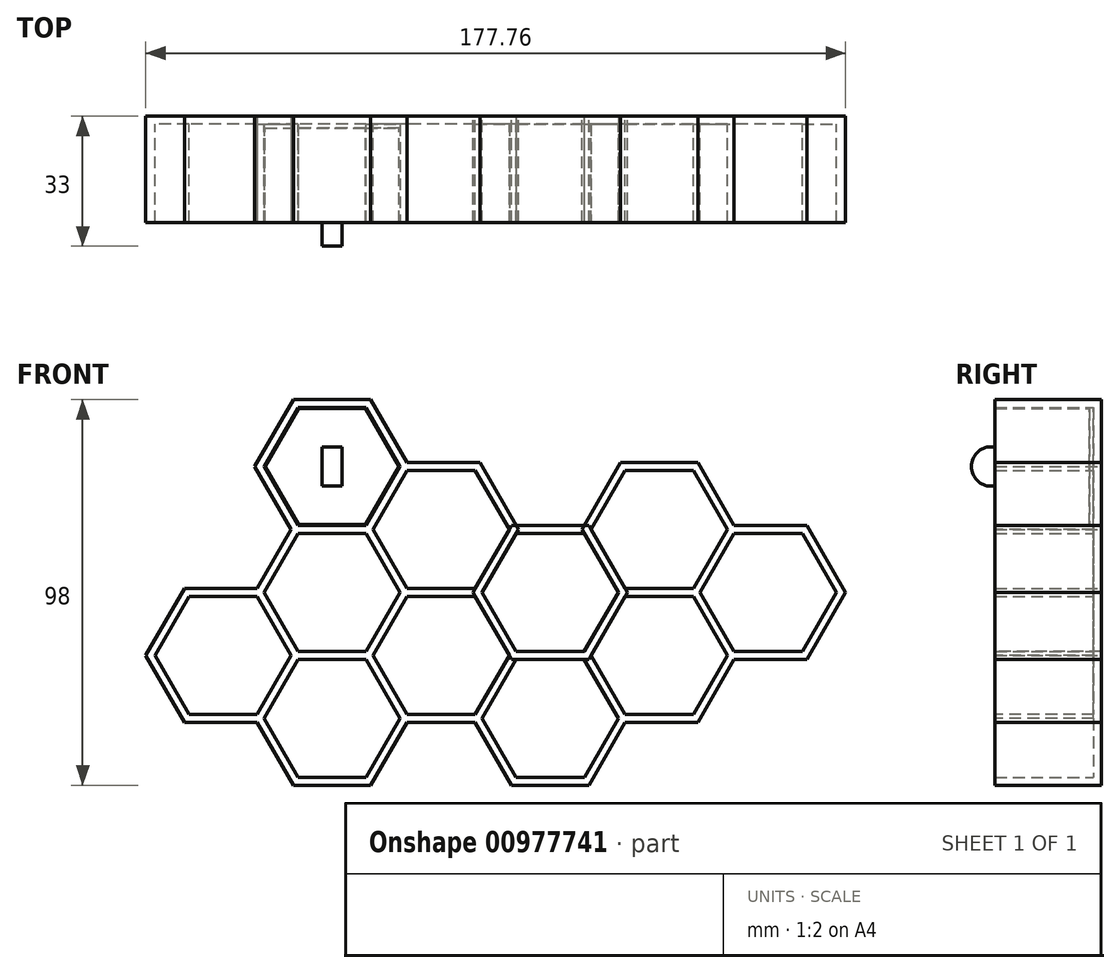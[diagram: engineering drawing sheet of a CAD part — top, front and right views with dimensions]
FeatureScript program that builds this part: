
annotation { "Feature Type Name" : "Feature", "Feature Type Description" : "" }
export const myFeature = defineFeature(function(context is Context, id is Id, definition is map)
    precondition{}
    {
        {
            var Q0;
            Q0=qCreatedBy(makeId("Front.planeOp"),FACE);
            var sketch = newSketch(context, id + "F0", { "sketchPlane" : qUnion([Q0])});
            skCircle(sketch, "E0.cCircle", {"center": v(0, 0) * mm, "radius": 15 * mm, "construction": true});
            skLineSegment(sketch, "E0.0", {"start": v(17.32, 0) * mm, "end": v(8.66, -15) * mm});
            skLineSegment(sketch, "E0.1", {"start": v(8.66, -15) * mm, "end": v(-8.66, -15) * mm});
            skLineSegment(sketch, "E0.2", {"start": v(-8.66, -15) * mm, "end": v(-17.32, 0) * mm});
            skLineSegment(sketch, "E0.3", {"start": v(-17.32, 0) * mm, "end": v(-8.66, 15) * mm});
            skLineSegment(sketch, "E0.4", {"start": v(-8.66, 15) * mm, "end": v(8.66, 15) * mm});
            skLineSegment(sketch, "E0.5", {"start": v(8.66, 15) * mm, "end": v(17.32, 0) * mm});
            skPoint(sketch, "E0.0.midPoint", {"position": v(13, -7.5) * mm});
            skLineSegment(sketch, "E1.0", {"start": v(-9.81, 17) * mm, "end": v(9.81, 17) * mm});
            skLineSegment(sketch, "E1.1", {"start": v(19.63, 0) * mm, "end": v(9.81, -17) * mm});
            skLineSegment(sketch, "E1.2", {"start": v(9.81, -17) * mm, "end": v(-9.81, -17) * mm});
            skLineSegment(sketch, "E1.3", {"start": v(9.81, 17) * mm, "end": v(19.63, 0) * mm});
            skLineSegment(sketch, "E1.4", {"start": v(-9.81, -17) * mm, "end": v(-19.63, 0) * mm});
            skLineSegment(sketch, "E1.5", {"start": v(-19.63, 0) * mm, "end": v(-9.81, 17) * mm});
            skSolve(sketch);
        }
        {
            var Q0;
            Q0 = qSketchRegion(id + "F0", true);
            extrude(context, id + "F1", {"entities" : qUnion([Q0]), "depth" : 25 * mm, "offsetDistance" : 25 * mm});
        }
        {
            var Q0;
            Q0=makeQuery(id+"F1.opExtrude","CAP_FACE",FACE,{"disambiguationData":[OSD([sQuery(id+"F0.wireOp",EDGE,"E0.0"),sQuery(id+"F0.wireOp",EDGE,"E0.1"),sQuery(id+"F0.wireOp",EDGE,"E0.2"),sQuery(id+"F0.wireOp",EDGE,"E0.3"),sQuery(id+"F0.wireOp",EDGE,"E0.4"),sQuery(id+"F0.wireOp",EDGE,"E0.5"),sQuery(id+"F0.wireOp",EDGE,"E1.0"),sQuery(id+"F0.wireOp",EDGE,"E1.1"),sQuery(id+"F0.wireOp",EDGE,"E1.2"),sQuery(id+"F0.wireOp",EDGE,"E1.3"),sQuery(id+"F0.wireOp",EDGE,"E1.4"),sQuery(id+"F0.wireOp",EDGE,"E1.5")])],"isStart":true});
            var Q1;
            Q1=makeQuery(id+"F0.imprint","IMPRINT",FACE,{"disambiguationData":[TD([[makeQuery(id+"F0.imprint","IMPRINT",EDGE,{"derivedFrom":sQuery(id+"F0.wireOp",EDGE,"E0.0")}),-1.0]])]});
            extrude(context, id + "F2", {"entities" : qUnion([Q0, Q1]), "operationType" : NewBodyOperationType.ADD, "depth" : 2 * mm, "offsetDistance" : 25 * mm});
        }
        {
            var Q0;
            Q0=makeQuery(id+"F1.opExtrude","SWEPT_BODY",BODY,{"disambiguationData":[OSD([sQuery(id+"F0.wireOp",EDGE,"E0.0"),sQuery(id+"F0.wireOp",EDGE,"E0.1"),sQuery(id+"F0.wireOp",EDGE,"E0.2"),sQuery(id+"F0.wireOp",EDGE,"E0.3"),sQuery(id+"F0.wireOp",EDGE,"E0.4"),sQuery(id+"F0.wireOp",EDGE,"E0.5"),sQuery(id+"F0.wireOp",EDGE,"E1.0"),sQuery(id+"F0.wireOp",EDGE,"E1.1"),sQuery(id+"F0.wireOp",EDGE,"E1.2"),sQuery(id+"F0.wireOp",EDGE,"E1.3"),sQuery(id+"F0.wireOp",EDGE,"E1.4"),sQuery(id+"F0.wireOp",EDGE,"E1.5")])]});
            transform(context, id + "F3", {"entities" : qUnion([Q0]), "transformType" : TransformType.TRANSLATION_3D, "dx" : 27.7 * mm, "dy" : 0 * mm, "dz" : 16 * mm, "makeCopy" : true});
        }
        {
            var Q0;
            Q0=makeQuery(id+"F1.opExtrude","SWEPT_BODY",BODY,{"disambiguationData":[OSD([sQuery(id+"F0.wireOp",EDGE,"E0.0"),sQuery(id+"F0.wireOp",EDGE,"E0.1"),sQuery(id+"F0.wireOp",EDGE,"E0.2"),sQuery(id+"F0.wireOp",EDGE,"E0.3"),sQuery(id+"F0.wireOp",EDGE,"E0.4"),sQuery(id+"F0.wireOp",EDGE,"E0.5"),sQuery(id+"F0.wireOp",EDGE,"E1.0"),sQuery(id+"F0.wireOp",EDGE,"E1.1"),sQuery(id+"F0.wireOp",EDGE,"E1.2"),sQuery(id+"F0.wireOp",EDGE,"E1.3"),sQuery(id+"F0.wireOp",EDGE,"E1.4"),sQuery(id+"F0.wireOp",EDGE,"E1.5")])]});
            transform(context, id + "F4", {"entities" : qUnion([Q0]), "transformType" : TransformType.TRANSLATION_3D, "dx" : 27.7 * mm, "dy" : 0 * mm, "dz" : -16 * mm, "makeCopy" : true});
        }
        {
            var Q0;
            Q0=makeQuery(id+"F1.opExtrude","SWEPT_BODY",BODY,{"disambiguationData":[OSD([sQuery(id+"F0.wireOp",EDGE,"E0.0"),sQuery(id+"F0.wireOp",EDGE,"E0.1"),sQuery(id+"F0.wireOp",EDGE,"E0.2"),sQuery(id+"F0.wireOp",EDGE,"E0.3"),sQuery(id+"F0.wireOp",EDGE,"E0.4"),sQuery(id+"F0.wireOp",EDGE,"E0.5"),sQuery(id+"F0.wireOp",EDGE,"E1.0"),sQuery(id+"F0.wireOp",EDGE,"E1.1"),sQuery(id+"F0.wireOp",EDGE,"E1.2"),sQuery(id+"F0.wireOp",EDGE,"E1.3"),sQuery(id+"F0.wireOp",EDGE,"E1.4"),sQuery(id+"F0.wireOp",EDGE,"E1.5")])]});
            transform(context, id + "F5", {"entities" : qUnion([Q0]), "transformType" : TransformType.TRANSLATION_3D, "dx" : -27.7 * mm, "dy" : 0 * mm, "dz" : -16 * mm, "makeCopy" : true});
        }
        {
            var Q0;
            Q0=makeQuery(id+"F1.opExtrude","SWEPT_BODY",BODY,{"disambiguationData":[OSD([sQuery(id+"F0.wireOp",EDGE,"E0.0"),sQuery(id+"F0.wireOp",EDGE,"E0.1"),sQuery(id+"F0.wireOp",EDGE,"E0.2"),sQuery(id+"F0.wireOp",EDGE,"E0.3"),sQuery(id+"F0.wireOp",EDGE,"E0.4"),sQuery(id+"F0.wireOp",EDGE,"E0.5"),sQuery(id+"F0.wireOp",EDGE,"E1.0"),sQuery(id+"F0.wireOp",EDGE,"E1.1"),sQuery(id+"F0.wireOp",EDGE,"E1.2"),sQuery(id+"F0.wireOp",EDGE,"E1.3"),sQuery(id+"F0.wireOp",EDGE,"E1.4"),sQuery(id+"F0.wireOp",EDGE,"E1.5")])]});
            transform(context, id + "F6", {"entities" : qUnion([Q0]), "transformType" : TransformType.TRANSLATION_3D, "dx" : -27.7 * mm, "dy" : 0 * mm, "dz" : 16 * mm, "makeCopy" : true});
        }
        {
            var Q0;
            Q0=makeQuery(id+"F1.opExtrude","SWEPT_BODY",BODY,{"disambiguationData":[OSD([sQuery(id+"F0.wireOp",EDGE,"E0.0"),sQuery(id+"F0.wireOp",EDGE,"E0.1"),sQuery(id+"F0.wireOp",EDGE,"E0.2"),sQuery(id+"F0.wireOp",EDGE,"E0.3"),sQuery(id+"F0.wireOp",EDGE,"E0.4"),sQuery(id+"F0.wireOp",EDGE,"E0.5"),sQuery(id+"F0.wireOp",EDGE,"E1.0"),sQuery(id+"F0.wireOp",EDGE,"E1.1"),sQuery(id+"F0.wireOp",EDGE,"E1.2"),sQuery(id+"F0.wireOp",EDGE,"E1.3"),sQuery(id+"F0.wireOp",EDGE,"E1.4"),sQuery(id+"F0.wireOp",EDGE,"E1.5")])]});
            transform(context, id + "F7", {"entities" : qUnion([Q0]), "transformType" : TransformType.TRANSLATION_3D, "dx" : 0 * mm, "dy" : 0 * mm, "dz" : 32 * mm, "makeCopy" : true});
        }
        {
            var Q0;
            Q0=makeQuery(id+"F3.opPattern","COPY",BODY,{"derivedFrom":makeQuery(id+"F1.opExtrude","SWEPT_BODY",BODY,{"disambiguationData":[OSD([sQuery(id+"F0.wireOp",EDGE,"E0.0"),sQuery(id+"F0.wireOp",EDGE,"E0.1"),sQuery(id+"F0.wireOp",EDGE,"E0.2"),sQuery(id+"F0.wireOp",EDGE,"E0.3"),sQuery(id+"F0.wireOp",EDGE,"E0.4"),sQuery(id+"F0.wireOp",EDGE,"E0.5"),sQuery(id+"F0.wireOp",EDGE,"E1.0"),sQuery(id+"F0.wireOp",EDGE,"E1.1"),sQuery(id+"F0.wireOp",EDGE,"E1.2"),sQuery(id+"F0.wireOp",EDGE,"E1.3"),sQuery(id+"F0.wireOp",EDGE,"E1.4"),sQuery(id+"F0.wireOp",EDGE,"E1.5")])]}),"instanceName":"1"});
            transform(context, id + "F8", {"entities" : qUnion([Q0]), "transformType" : TransformType.TRANSLATION_3D, "dx" : 27.7 * mm, "dy" : 0 * mm, "dz" : -16 * mm, "makeCopy" : true});
        }
        {
            var Q0;
            Q0=makeQuery(id+"F7.opPattern","COPY",BODY,{"derivedFrom":makeQuery(id+"F1.opExtrude","SWEPT_BODY",BODY,{"disambiguationData":[OSD([sQuery(id+"F0.wireOp",EDGE,"E0.0"),sQuery(id+"F0.wireOp",EDGE,"E0.1"),sQuery(id+"F0.wireOp",EDGE,"E0.2"),sQuery(id+"F0.wireOp",EDGE,"E0.3"),sQuery(id+"F0.wireOp",EDGE,"E0.4"),sQuery(id+"F0.wireOp",EDGE,"E0.5"),sQuery(id+"F0.wireOp",EDGE,"E1.0"),sQuery(id+"F0.wireOp",EDGE,"E1.1"),sQuery(id+"F0.wireOp",EDGE,"E1.2"),sQuery(id+"F0.wireOp",EDGE,"E1.3"),sQuery(id+"F0.wireOp",EDGE,"E1.4"),sQuery(id+"F0.wireOp",EDGE,"E1.5")])]}),"instanceName":"1"});
            transform(context, id + "F9", {"entities" : qUnion([Q0]), "transformType" : TransformType.TRANSLATION_3D, "dx" : -27.7 * mm, "dy" : 0 * mm, "dz" : 16 * mm, "makeCopy" : true});
        }
        {
            var Q0;
            Q0=makeQuery(id+"F3.opPattern","COPY",BODY,{"derivedFrom":makeQuery(id+"F1.opExtrude","SWEPT_BODY",BODY,{"disambiguationData":[OSD([sQuery(id+"F0.wireOp",EDGE,"E0.0"),sQuery(id+"F0.wireOp",EDGE,"E0.1"),sQuery(id+"F0.wireOp",EDGE,"E0.2"),sQuery(id+"F0.wireOp",EDGE,"E0.3"),sQuery(id+"F0.wireOp",EDGE,"E0.4"),sQuery(id+"F0.wireOp",EDGE,"E0.5"),sQuery(id+"F0.wireOp",EDGE,"E1.0"),sQuery(id+"F0.wireOp",EDGE,"E1.1"),sQuery(id+"F0.wireOp",EDGE,"E1.2"),sQuery(id+"F0.wireOp",EDGE,"E1.3"),sQuery(id+"F0.wireOp",EDGE,"E1.4"),sQuery(id+"F0.wireOp",EDGE,"E1.5")])]}),"instanceName":"1"});
            transform(context, id + "F10", {"entities" : qUnion([Q0]), "transformType" : TransformType.TRANSLATION_3D, "dx" : 27.7 * mm, "dy" : 0 * mm, "dz" : 16 * mm, "makeCopy" : true});
        }
        {
            var Q0;
            Q0=makeQuery(id+"F6.opPattern","COPY",BODY,{"derivedFrom":makeQuery(id+"F1.opExtrude","SWEPT_BODY",BODY,{"disambiguationData":[OSD([sQuery(id+"F0.wireOp",EDGE,"E0.0"),sQuery(id+"F0.wireOp",EDGE,"E0.1"),sQuery(id+"F0.wireOp",EDGE,"E0.2"),sQuery(id+"F0.wireOp",EDGE,"E0.3"),sQuery(id+"F0.wireOp",EDGE,"E0.4"),sQuery(id+"F0.wireOp",EDGE,"E0.5"),sQuery(id+"F0.wireOp",EDGE,"E1.0"),sQuery(id+"F0.wireOp",EDGE,"E1.1"),sQuery(id+"F0.wireOp",EDGE,"E1.2"),sQuery(id+"F0.wireOp",EDGE,"E1.3"),sQuery(id+"F0.wireOp",EDGE,"E1.4"),sQuery(id+"F0.wireOp",EDGE,"E1.5")])]}),"instanceName":"1"});
            transform(context, id + "F11", {"entities" : qUnion([Q0]), "transformType" : TransformType.TRANSLATION_3D, "dx" : -27.7 * mm, "dy" : 0 * mm, "dz" : -16 * mm, "makeCopy" : true});
        }
        {
            var Q0;
            Q0=makeQuery(id+"F10.opPattern","COPY",BODY,{"derivedFrom":makeQuery(id+"F3.opPattern","COPY",BODY,{"derivedFrom":makeQuery(id+"F1.opExtrude","SWEPT_BODY",BODY,{"disambiguationData":[OSD([sQuery(id+"F0.wireOp",EDGE,"E0.0"),sQuery(id+"F0.wireOp",EDGE,"E0.1"),sQuery(id+"F0.wireOp",EDGE,"E0.2"),sQuery(id+"F0.wireOp",EDGE,"E0.3"),sQuery(id+"F0.wireOp",EDGE,"E0.4"),sQuery(id+"F0.wireOp",EDGE,"E0.5"),sQuery(id+"F0.wireOp",EDGE,"E1.0"),sQuery(id+"F0.wireOp",EDGE,"E1.1"),sQuery(id+"F0.wireOp",EDGE,"E1.2"),sQuery(id+"F0.wireOp",EDGE,"E1.3"),sQuery(id+"F0.wireOp",EDGE,"E1.4"),sQuery(id+"F0.wireOp",EDGE,"E1.5")])]}),"instanceName":"1"}),"instanceName":"1"});
            transform(context, id + "F12", {"entities" : qUnion([Q0]), "transformType" : TransformType.TRANSLATION_3D, "dx" : 27.7 * mm, "dy" : 0 * mm, "dz" : -16 * mm, "makeCopy" : true});
        }
        {
            var Q0;
            Q0=makeQuery(id+"F1.opExtrude","SWEPT_BODY",BODY,{"disambiguationData":[OSD([sQuery(id+"F0.wireOp",EDGE,"E0.0"),sQuery(id+"F0.wireOp",EDGE,"E0.1"),sQuery(id+"F0.wireOp",EDGE,"E0.2"),sQuery(id+"F0.wireOp",EDGE,"E0.3"),sQuery(id+"F0.wireOp",EDGE,"E0.4"),sQuery(id+"F0.wireOp",EDGE,"E0.5"),sQuery(id+"F0.wireOp",EDGE,"E1.0"),sQuery(id+"F0.wireOp",EDGE,"E1.1"),sQuery(id+"F0.wireOp",EDGE,"E1.2"),sQuery(id+"F0.wireOp",EDGE,"E1.3"),sQuery(id+"F0.wireOp",EDGE,"E1.4"),sQuery(id+"F0.wireOp",EDGE,"E1.5")])]});
            var Q1;
            Q1=makeQuery(id+"F4.opPattern","COPY",BODY,{"derivedFrom":makeQuery(id+"F1.opExtrude","SWEPT_BODY",BODY,{"disambiguationData":[OSD([sQuery(id+"F0.wireOp",EDGE,"E0.0"),sQuery(id+"F0.wireOp",EDGE,"E0.1"),sQuery(id+"F0.wireOp",EDGE,"E0.2"),sQuery(id+"F0.wireOp",EDGE,"E0.3"),sQuery(id+"F0.wireOp",EDGE,"E0.4"),sQuery(id+"F0.wireOp",EDGE,"E0.5"),sQuery(id+"F0.wireOp",EDGE,"E1.0"),sQuery(id+"F0.wireOp",EDGE,"E1.1"),sQuery(id+"F0.wireOp",EDGE,"E1.2"),sQuery(id+"F0.wireOp",EDGE,"E1.3"),sQuery(id+"F0.wireOp",EDGE,"E1.4"),sQuery(id+"F0.wireOp",EDGE,"E1.5")])]}),"instanceName":"1"});
            var Q2;
            Q2=makeQuery(id+"F5.opPattern","COPY",BODY,{"derivedFrom":makeQuery(id+"F1.opExtrude","SWEPT_BODY",BODY,{"disambiguationData":[OSD([sQuery(id+"F0.wireOp",EDGE,"E0.0"),sQuery(id+"F0.wireOp",EDGE,"E0.1"),sQuery(id+"F0.wireOp",EDGE,"E0.2"),sQuery(id+"F0.wireOp",EDGE,"E0.3"),sQuery(id+"F0.wireOp",EDGE,"E0.4"),sQuery(id+"F0.wireOp",EDGE,"E0.5"),sQuery(id+"F0.wireOp",EDGE,"E1.0"),sQuery(id+"F0.wireOp",EDGE,"E1.1"),sQuery(id+"F0.wireOp",EDGE,"E1.2"),sQuery(id+"F0.wireOp",EDGE,"E1.3"),sQuery(id+"F0.wireOp",EDGE,"E1.4"),sQuery(id+"F0.wireOp",EDGE,"E1.5")])]}),"instanceName":"1"});
            var Q3;
            Q3=makeQuery(id+"F6.opPattern","COPY",BODY,{"derivedFrom":makeQuery(id+"F1.opExtrude","SWEPT_BODY",BODY,{"disambiguationData":[OSD([sQuery(id+"F0.wireOp",EDGE,"E0.0"),sQuery(id+"F0.wireOp",EDGE,"E0.1"),sQuery(id+"F0.wireOp",EDGE,"E0.2"),sQuery(id+"F0.wireOp",EDGE,"E0.3"),sQuery(id+"F0.wireOp",EDGE,"E0.4"),sQuery(id+"F0.wireOp",EDGE,"E0.5"),sQuery(id+"F0.wireOp",EDGE,"E1.0"),sQuery(id+"F0.wireOp",EDGE,"E1.1"),sQuery(id+"F0.wireOp",EDGE,"E1.2"),sQuery(id+"F0.wireOp",EDGE,"E1.3"),sQuery(id+"F0.wireOp",EDGE,"E1.4"),sQuery(id+"F0.wireOp",EDGE,"E1.5")])]}),"instanceName":"1"});
            var Q4;
            Q4=makeQuery(id+"F7.opPattern","COPY",BODY,{"derivedFrom":makeQuery(id+"F1.opExtrude","SWEPT_BODY",BODY,{"disambiguationData":[OSD([sQuery(id+"F0.wireOp",EDGE,"E0.0"),sQuery(id+"F0.wireOp",EDGE,"E0.1"),sQuery(id+"F0.wireOp",EDGE,"E0.2"),sQuery(id+"F0.wireOp",EDGE,"E0.3"),sQuery(id+"F0.wireOp",EDGE,"E0.4"),sQuery(id+"F0.wireOp",EDGE,"E0.5"),sQuery(id+"F0.wireOp",EDGE,"E1.0"),sQuery(id+"F0.wireOp",EDGE,"E1.1"),sQuery(id+"F0.wireOp",EDGE,"E1.2"),sQuery(id+"F0.wireOp",EDGE,"E1.3"),sQuery(id+"F0.wireOp",EDGE,"E1.4"),sQuery(id+"F0.wireOp",EDGE,"E1.5")])]}),"instanceName":"1"});
            var Q5;
            Q5=makeQuery(id+"F9.opPattern","COPY",BODY,{"derivedFrom":makeQuery(id+"F7.opPattern","COPY",BODY,{"derivedFrom":makeQuery(id+"F1.opExtrude","SWEPT_BODY",BODY,{"disambiguationData":[OSD([sQuery(id+"F0.wireOp",EDGE,"E0.0"),sQuery(id+"F0.wireOp",EDGE,"E0.1"),sQuery(id+"F0.wireOp",EDGE,"E0.2"),sQuery(id+"F0.wireOp",EDGE,"E0.3"),sQuery(id+"F0.wireOp",EDGE,"E0.4"),sQuery(id+"F0.wireOp",EDGE,"E0.5"),sQuery(id+"F0.wireOp",EDGE,"E1.0"),sQuery(id+"F0.wireOp",EDGE,"E1.1"),sQuery(id+"F0.wireOp",EDGE,"E1.2"),sQuery(id+"F0.wireOp",EDGE,"E1.3"),sQuery(id+"F0.wireOp",EDGE,"E1.4"),sQuery(id+"F0.wireOp",EDGE,"E1.5")])]}),"instanceName":"1"}),"instanceName":"1"});
            var Q6;
            Q6=makeQuery(id+"F8.opPattern","COPY",BODY,{"derivedFrom":makeQuery(id+"F3.opPattern","COPY",BODY,{"derivedFrom":makeQuery(id+"F1.opExtrude","SWEPT_BODY",BODY,{"disambiguationData":[OSD([sQuery(id+"F0.wireOp",EDGE,"E0.0"),sQuery(id+"F0.wireOp",EDGE,"E0.1"),sQuery(id+"F0.wireOp",EDGE,"E0.2"),sQuery(id+"F0.wireOp",EDGE,"E0.3"),sQuery(id+"F0.wireOp",EDGE,"E0.4"),sQuery(id+"F0.wireOp",EDGE,"E0.5"),sQuery(id+"F0.wireOp",EDGE,"E1.0"),sQuery(id+"F0.wireOp",EDGE,"E1.1"),sQuery(id+"F0.wireOp",EDGE,"E1.2"),sQuery(id+"F0.wireOp",EDGE,"E1.3"),sQuery(id+"F0.wireOp",EDGE,"E1.4"),sQuery(id+"F0.wireOp",EDGE,"E1.5")])]}),"instanceName":"1"}),"instanceName":"1"});
            var Q7;
            Q7=makeQuery(id+"F10.opPattern","COPY",BODY,{"derivedFrom":makeQuery(id+"F3.opPattern","COPY",BODY,{"derivedFrom":makeQuery(id+"F1.opExtrude","SWEPT_BODY",BODY,{"disambiguationData":[OSD([sQuery(id+"F0.wireOp",EDGE,"E0.0"),sQuery(id+"F0.wireOp",EDGE,"E0.1"),sQuery(id+"F0.wireOp",EDGE,"E0.2"),sQuery(id+"F0.wireOp",EDGE,"E0.3"),sQuery(id+"F0.wireOp",EDGE,"E0.4"),sQuery(id+"F0.wireOp",EDGE,"E0.5"),sQuery(id+"F0.wireOp",EDGE,"E1.0"),sQuery(id+"F0.wireOp",EDGE,"E1.1"),sQuery(id+"F0.wireOp",EDGE,"E1.2"),sQuery(id+"F0.wireOp",EDGE,"E1.3"),sQuery(id+"F0.wireOp",EDGE,"E1.4"),sQuery(id+"F0.wireOp",EDGE,"E1.5")])]}),"instanceName":"1"}),"instanceName":"1"});
            var Q8;
            Q8=makeQuery(id+"F11.opPattern","COPY",BODY,{"derivedFrom":makeQuery(id+"F6.opPattern","COPY",BODY,{"derivedFrom":makeQuery(id+"F1.opExtrude","SWEPT_BODY",BODY,{"disambiguationData":[OSD([sQuery(id+"F0.wireOp",EDGE,"E0.0"),sQuery(id+"F0.wireOp",EDGE,"E0.1"),sQuery(id+"F0.wireOp",EDGE,"E0.2"),sQuery(id+"F0.wireOp",EDGE,"E0.3"),sQuery(id+"F0.wireOp",EDGE,"E0.4"),sQuery(id+"F0.wireOp",EDGE,"E0.5"),sQuery(id+"F0.wireOp",EDGE,"E1.0"),sQuery(id+"F0.wireOp",EDGE,"E1.1"),sQuery(id+"F0.wireOp",EDGE,"E1.2"),sQuery(id+"F0.wireOp",EDGE,"E1.3"),sQuery(id+"F0.wireOp",EDGE,"E1.4"),sQuery(id+"F0.wireOp",EDGE,"E1.5")])]}),"instanceName":"1"}),"instanceName":"1"});
            var Q9;
            Q9=makeQuery(id+"F12.opPattern","COPY",BODY,{"derivedFrom":makeQuery(id+"F10.opPattern","COPY",BODY,{"derivedFrom":makeQuery(id+"F3.opPattern","COPY",BODY,{"derivedFrom":makeQuery(id+"F1.opExtrude","SWEPT_BODY",BODY,{"disambiguationData":[OSD([sQuery(id+"F0.wireOp",EDGE,"E0.0"),sQuery(id+"F0.wireOp",EDGE,"E0.1"),sQuery(id+"F0.wireOp",EDGE,"E0.2"),sQuery(id+"F0.wireOp",EDGE,"E0.3"),sQuery(id+"F0.wireOp",EDGE,"E0.4"),sQuery(id+"F0.wireOp",EDGE,"E0.5"),sQuery(id+"F0.wireOp",EDGE,"E1.0"),sQuery(id+"F0.wireOp",EDGE,"E1.1"),sQuery(id+"F0.wireOp",EDGE,"E1.2"),sQuery(id+"F0.wireOp",EDGE,"E1.3"),sQuery(id+"F0.wireOp",EDGE,"E1.4"),sQuery(id+"F0.wireOp",EDGE,"E1.5")])]}),"instanceName":"1"}),"instanceName":"1"}),"instanceName":"1"});
            booleanBodies(context, id + "F13", {"operationType" : BooleanOperationType.UNION, "tools" : qUnion([Q0, Q1, Q2, Q3, Q4, Q5, Q6, Q7, Q8, Q9])});
        }
        {
            var Q0;
            {var subQ0=sQuery(id+"F0.wireOp",EDGE,"E0.5");var subQ1=sQuery(id+"F0.wireOp",EDGE,"E0.4");var subQ2=sQuery(id+"F0.wireOp",EDGE,"E0.3");var subQ3=sQuery(id+"F0.wireOp",EDGE,"E0.2");var subQ4=sQuery(id+"F0.wireOp",EDGE,"E0.1");var subQ5=sQuery(id+"F0.wireOp",EDGE,"E0.0");Q0=makeQuery(id+"F9.opPattern","COPY",FACE,{"derivedFrom":makeQuery(id+"F7.opPattern","COPY",FACE,{"derivedFrom":makeQuery(id+"F2.boolean.opBoolean","MERGE",FACE,{"derivedFrom":[makeQuery(id+"F2.opExtrude","CAP_FACE",FACE,{"disambiguationData":[OSD([subQ5,subQ4,subQ3,subQ2,subQ1,subQ0])],"isStart":true}),makeQuery(id+"F2.opExtrude","CAP_FACE",FACE,{"disambiguationData":[OSD([subQ5,subQ4,subQ3,subQ2,subQ1,subQ0,sQuery(id+"F0.wireOp",EDGE,"E1.0"),sQuery(id+"F0.wireOp",EDGE,"E1.1"),sQuery(id+"F0.wireOp",EDGE,"E1.2"),sQuery(id+"F0.wireOp",EDGE,"E1.3"),sQuery(id+"F0.wireOp",EDGE,"E1.4"),sQuery(id+"F0.wireOp",EDGE,"E1.5")])],"isStart":true})]}),"instanceName":"1"}),"instanceName":"1"});}
            var sketch = newSketch(context, id + "F14", { "sketchPlane" : qUnion([Q0])});
            skLineSegment(sketch, "E2.0", {"start": v(-44.73, 48) * mm, "end": v(-36.22, 33.25) * mm});
            skLineSegment(sketch, "E2.1", {"start": v(-19.2, 33.25) * mm, "end": v(-10.67, 48.01) * mm});
            skLineSegment(sketch, "E2.2", {"start": v(-10.67, 48.01) * mm, "end": v(-19.18, 62.75) * mm});
            skLineSegment(sketch, "E2.3", {"start": v(-36.22, 33.25) * mm, "end": v(-19.2, 33.25) * mm});
            skLineSegment(sketch, "E2.4", {"start": v(-19.18, 62.75) * mm, "end": v(-36.22, 62.75) * mm});
            skLineSegment(sketch, "E2.5", {"start": v(-36.22, 62.75) * mm, "end": v(-44.73, 48) * mm});
            skSolve(sketch);
        }
        {
            var Q0;
            Q0=makeQuery(id+"F14.imprint","IMPRINT",FACE,{"disambiguationData":[TD([[makeQuery(id+"F14.imprint","IMPRINT",EDGE,{"derivedFrom":sQuery(id+"F14.wireOp",EDGE,"E2.0")}),1.0]])]});
            extrude(context, id + "F15", {"entities" : qUnion([Q0]), "depth" : 25 * mm, "offsetDistance" : 25 * mm});
        }
        {
            var Q0;
            Q0=makeQuery(id+"F15.opExtrude","CAP_FACE",FACE,{"disambiguationData":[OSD([sQuery(id+"F14.wireOp",EDGE,"E2.0"),sQuery(id+"F14.wireOp",EDGE,"E2.1"),sQuery(id+"F14.wireOp",EDGE,"E2.2"),sQuery(id+"F14.wireOp",EDGE,"E2.3"),sQuery(id+"F14.wireOp",EDGE,"E2.4"),sQuery(id+"F14.wireOp",EDGE,"E2.5")])],"isStart":false});
            var sketch = newSketch(context, id + "F16", { "sketchPlane" : qUnion([Q0])});
            skLineSegment(sketch, "E3", {"start": v(-36.22, 62.75) * mm, "end": v(-19.2, 33.25) * mm, "construction": true});
            skLineSegment(sketch, "E4", {"start": v(-36.22, 33.25) * mm, "end": v(-19.18, 62.75) * mm, "construction": true});
            skLineSegment(sketch, "E5.bottom", {"start": v(-25.2, 43) * mm, "end": v(-30.2, 43) * mm});
            skLineSegment(sketch, "E5.top", {"start": v(-25.2, 53) * mm, "end": v(-30.2, 53) * mm});
            skLineSegment(sketch, "E5.left", {"start": v(-25.2, 43) * mm, "end": v(-25.2, 53) * mm});
            skLineSegment(sketch, "E5.right", {"start": v(-30.2, 43) * mm, "end": v(-30.2, 53) * mm});
            skPoint(sketch, "E5.middle", {"position": v(-27.7, 48) * mm});
            skSolve(sketch);
        }
        {
            var Q0;
            Q0=makeQuery(id+"F16.imprint","IMPRINT",FACE,{"disambiguationData":[TD([[makeQuery(id+"F16.imprint","IMPRINT",EDGE,{"derivedFrom":sQuery(id+"F16.wireOp",EDGE,"E5.bottom")}),-1.0]])]});
            extrude(context, id + "F17", {"entities" : qUnion([Q0]), "operationType" : NewBodyOperationType.ADD, "depth" : 6 * mm, "offsetDistance" : 25 * mm});
        }
        {
            var Q0;
            Q0=makeQuery(id+"F17.opExtrude","CAP_EDGE",EDGE,{"disambiguationData":[OSD([sQuery(id+"F16.wireOp",EDGE,"E5.top")])],"isStart":false});
            var Q1;
            Q1=makeQuery(id+"F17.opExtrude","CAP_EDGE",EDGE,{"disambiguationData":[OSD([sQuery(id+"F16.wireOp",EDGE,"E5.bottom")])],"isStart":false});
            fillet(context, id + "F18", {"entities" : qUnion([Q0, Q1]), "radius" : 5 * mm, "tangentPropagation" : true, "allowEdgeOverflow" : false});
        }
        {
            var Q0;
            Q0=makeQuery(id+"F15.opExtrude","CAP_FACE",FACE,{"disambiguationData":[OSD([sQuery(id+"F14.wireOp",EDGE,"E2.0"),sQuery(id+"F14.wireOp",EDGE,"E2.1"),sQuery(id+"F14.wireOp",EDGE,"E2.2"),sQuery(id+"F14.wireOp",EDGE,"E2.3"),sQuery(id+"F14.wireOp",EDGE,"E2.4"),sQuery(id+"F14.wireOp",EDGE,"E2.5")])],"isStart":true});
            extrude(context, id + "F19", {"entities" : qUnion([Q0]), "operationType" : NewBodyOperationType.REMOVE, "oppositeDirection" : true, "depth" : 1 * mm, "offsetDistance" : 25 * mm});
        }
    });
